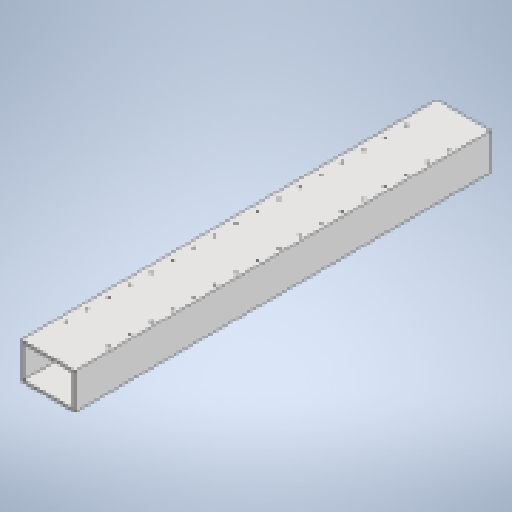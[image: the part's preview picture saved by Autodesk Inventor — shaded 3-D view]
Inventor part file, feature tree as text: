
AUTODESK INVENTOR PART (.ipt)
format: ipt  version: 2023 (Build 270158000, 158)  size: 185,344 bytes
history: native  units: in
note: dims shown in document units (in); Inventor stores cm internally (conversion verified against a paired STEP export)
features: other x4, extrude x2, sketch x2, reference x2, shell x1
ambient origin geometry x8: Origin, YZ Plane, XZ Plane, XY Plane, X Axis, Y Axis, Z Axis, Center Point
bodies: Solid1 (feature_tree)
feature tree (11):
  extrude  "Extrusion1"  Depth=4.0in
  shell  "Shell1"  Thickness=46.232in
  extrude  "Extrusion2"  Depth=46.232in TaperAngle=0.0deg
  sketch  "Sketch1"  dims[d0=6.0in d1=4.0in d2=46.232in d3=0.0in]
  sketch  "Sketch2"  dims[d4=0.25in d5=46.232in d6=0.0in]
  reference  "Reference1"
  reference  "Reference2"
  other  "<userpath>\Desktop\CNC_Project\FrameV2.iam"
  other  "FrameV2.iam"
  other  "HGW20CC_Rail_800mm:4"
  other  "HGW20CC_Rail_800mm:3"
